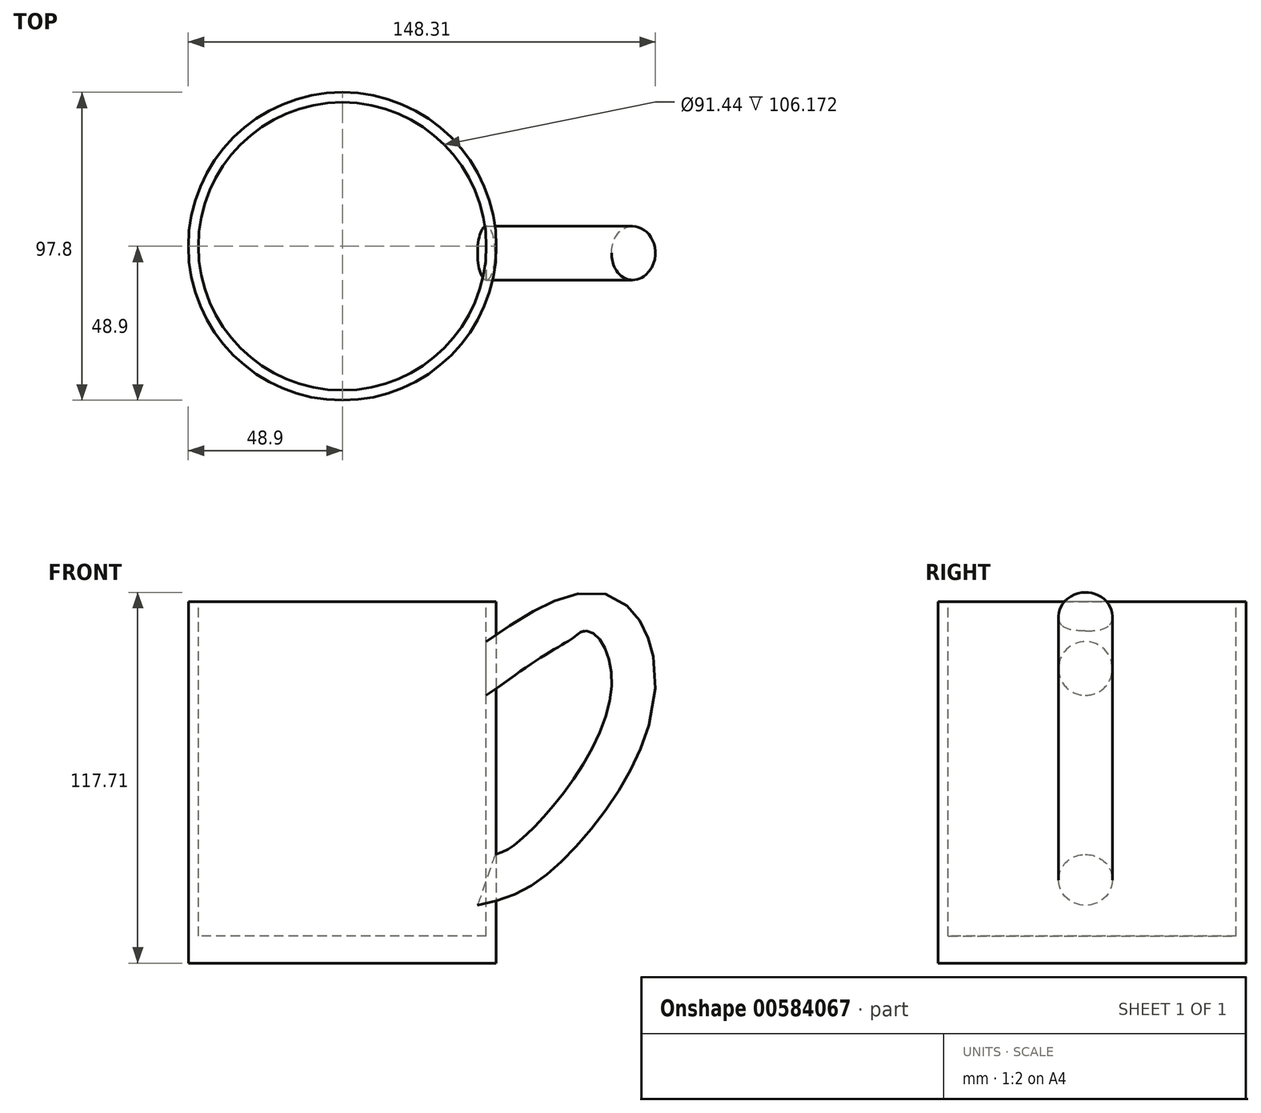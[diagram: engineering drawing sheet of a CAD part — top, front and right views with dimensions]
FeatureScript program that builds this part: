
annotation { "Feature Type Name" : "Feature", "Feature Type Description" : "" }
export const myFeature = defineFeature(function(context is Context, id is Id, definition is map)
    precondition{}
    {
        {
            var Q0;
            Q0=qCreatedBy(makeId("Top.planeOp"),FACE);
            var sketch = newSketch(context, id + "F0", { "sketchPlane" : qUnion([Q0])});
            skCircle(sketch, "E0", {"center": v(0, 0) * mm, "radius": 48.9 * mm});
            skSolve(sketch);
        }
        {
            var Q0;
            Q0=makeQuery(id+"F0.imprint","IMPRINT",FACE,{"disambiguationData":[TD([[makeQuery(id+"F0.imprint","IMPRINT",EDGE,{"derivedFrom":sQuery(id+"F0.wireOp",EDGE,"E0")}),1.0]])]});
            extrude(context, id + "F1", {"entities" : qUnion([Q0]), "depth" : 114.8 * mm, "offsetDistance" : 25.4 * mm});
        }
        {
            var Q0;
            Q0=makeQuery(id+"F1.opExtrude","CAP_FACE",FACE,{"disambiguationData":[OSD([sQuery(id+"F0.wireOp",EDGE,"E0")])],"isStart":false});
            var sketch = newSketch(context, id + "F2", { "sketchPlane" : qUnion([Q0])});
            skCircle(sketch, "E1", {"center": v(0, 0) * mm, "radius": 45.72 * mm});
            skSolve(sketch);
        }
        {
            var Q0;
            Q0=makeQuery(id+"F2.imprint","IMPRINT",FACE,{"disambiguationData":[TD([[makeQuery(id+"F2.imprint","IMPRINT",EDGE,{"derivedFrom":sQuery(id+"F2.wireOp",EDGE,"E1")}),1.0]])]});
            extrude(context, id + "F3", {"entities" : qUnion([Q0]), "operationType" : NewBodyOperationType.REMOVE, "oppositeDirection" : true, "depth" : 106.17 * mm, "offsetDistance" : 25.4 * mm});
        }
        {
            var Q0;
            Q0=qCreatedBy(makeId("Right.planeOp"),FACE);
            cPlane(context, id + "F4", {"entities" : qUnion([Q0]), "cplaneType" : CPlaneType.OFFSET, "offset" : 45.72 * mm, "width" : 152.4 * mm, "height" : 152.4 * mm});
        }
        {
            var Q0;
            Q0=qCreatedBy(id+"F4.planeOp",FACE);
            var sketch = newSketch(context, id + "F5", { "sketchPlane" : qUnion([Q0])});
            skCircle(sketch, "E2", {"center": v(-2.14, 93.56) * mm, "radius": 8.55 * mm});
            skSolve(sketch);
        }
        {
            var Q0;
            Q0=qCreatedBy(makeId("Front.planeOp"),FACE);
            var sketch = newSketch(context, id + "F6", { "sketchPlane" : qUnion([Q0])});
            skPoint(sketch, "E3.0", {"position": v(45.72, 93.56) * mm});
            skFitSpline(sketch, "E4", {"points": [v(45.72, 93.56) * mm, v(81.93, 109.65) * mm, v(91.4, 81.5) * mm, v(60.23, 33.54) * mm, v(45.72, 26.43) * mm], "startDerivative": vector(151.52, 106.54) * mm, "endDerivative": vector(-75.13, -21.56) * mm});
            skSolve(sketch);
        }
        {
            var Q0;
            Q0 = qSketchRegion(id + "F5", true);
            var Q1;
            Q1 = qConstructionFilter(qBodyType(qCreatedBy(id + "F6" ,EDGE), BodyType.WIRE), ConstructionObject.NO);
            sweep(context, id + "F7", {"profiles" : qUnion([Q0]), "path" : qUnion([Q1])});
        }
    });
